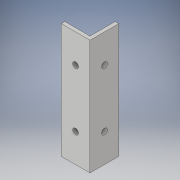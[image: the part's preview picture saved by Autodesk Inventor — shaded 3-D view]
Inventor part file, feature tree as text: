
AUTODESK INVENTOR PART (.ipt)
format: ipt  version: 2018 (Build 220112000, 112)  size: 123,392 bytes
history: native  units: in
note: dims shown in document units (in); Inventor stores cm internally (conversion verified against a paired STEP export)
features: extrude x3, sketch x3
ambient origin geometry x8: Origin, YZ Plane, XZ Plane, XY Plane, X Axis, Y Axis, Z Axis, Center Point
bodies: Solid1 (feature_tree)
feature tree (6):
  extrude  "Extrusion1"  Depth=0.125in
  extrude  "Extrusion2"  Depth=0.125in
  extrude  "Extrusion3"  Depth=1.0in
  sketch  "Sketch1"  dims[d0=1.0in d1=0.125in]
  sketch  "Sketch2"  dims[d2=1.0in d3=0.125in]
  sketch  "Sketch3"  dims[d4=4.0in d5=0.0in d6=0.5in d7=1.0in d8=1.0in d9=0.2in d10=1.0in d11=0.0in d12=1.0in d13=1.0in d14=0.2in d15=1.0in d16=0.0in]
